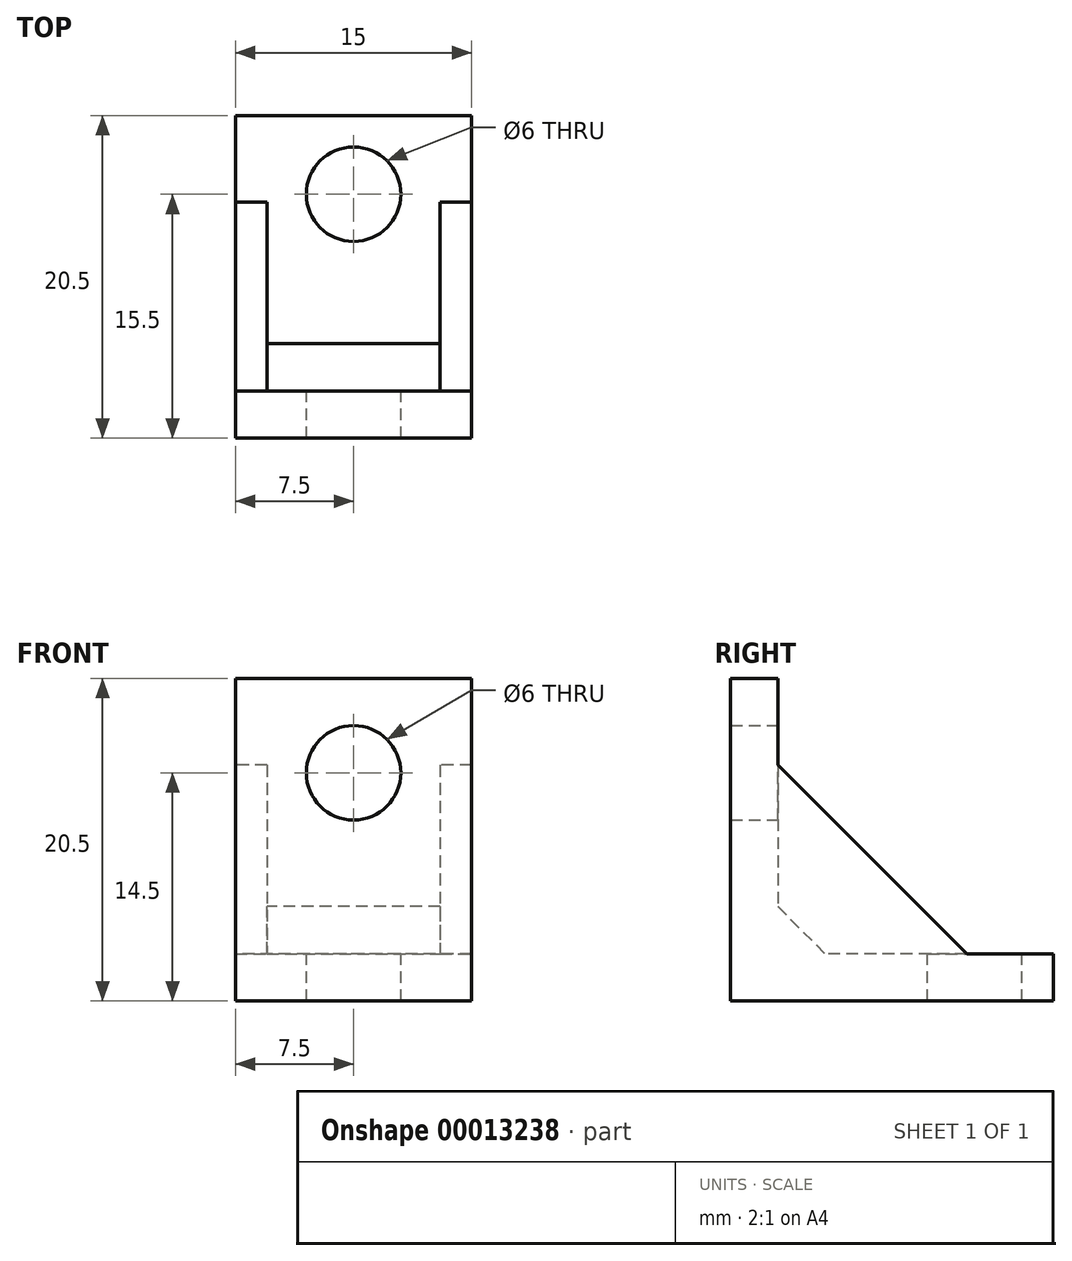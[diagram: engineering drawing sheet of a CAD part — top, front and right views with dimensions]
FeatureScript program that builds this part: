
annotation { "Feature Type Name" : "Feature", "Feature Type Description" : "" }
export const myFeature = defineFeature(function(context is Context, id is Id, definition is map)
    precondition{}
    {
        {
            var Q0;
            Q0=qCreatedBy(makeId("Right.planeOp"),FACE);
            var sketch = newSketch(context, id + "F0", { "sketchPlane" : qUnion([Q0])});
            skLineSegment(sketch, "E0", {"start": v(0, 20.5) * mm, "end": v(0, 0) * mm});
            skLineSegment(sketch, "E1", {"start": v(0, 0) * mm, "end": v(20.5, 0) * mm});
            skLineSegment(sketch, "E2", {"start": v(20.5, 0) * mm, "end": v(20.5, 3) * mm});
            skLineSegment(sketch, "E3", {"start": v(20.5, 3) * mm, "end": v(3, 3) * mm});
            skLineSegment(sketch, "E4", {"start": v(3, 3) * mm, "end": v(3, 20.5) * mm});
            skLineSegment(sketch, "E5", {"start": v(3, 20.5) * mm, "end": v(0, 20.5) * mm});
            skSolve(sketch);
        }
        {
            var Q0;
            Q0 = qSketchRegion(id + "F0", true);
            extrude(context, id + "F1", {"entities" : qUnion([Q0]), "depth" : 15 * mm});
        }
        {
            var Q0;
            Q0=makeQuery(id+"F1.opExtrude","SWEPT_FACE",FACE,{"disambiguationData":[OSD([sQuery(id+"F0.wireOp",EDGE,"E4")])]});
            var sketch = newSketch(context, id + "F2", { "sketchPlane" : qUnion([Q0])});
            skPoint(sketch, "E6", {"position": v(-7.5, 14.5) * mm});
            skPoint(sketch, "E7", {"position": v(-7.5, 20.5) * mm});
            skSolve(sketch);
        }
        {
            var Q0;
            Q0=makeQuery(id+"F1.opExtrude","SWEPT_FACE",FACE,{"disambiguationData":[OSD([sQuery(id+"F0.wireOp",EDGE,"E3")])]});
            var sketch = newSketch(context, id + "F3", { "sketchPlane" : qUnion([Q0])});
            skPoint(sketch, "E8", {"position": v(7.5, 15.5) * mm});
            skSolve(sketch);
        }
        {
            var Q0;
            Q0=sQuery(id+"F3.wireOp",VERTEX,"E8");
            var Q1;
            Q1=sQuery(id+"F2.wireOp",VERTEX,"E6");
            var Q2;
            Q2=makeQuery(id+"F1.opExtrude","SWEPT_BODY",BODY,{"disambiguationData":[OSD([sQuery(id+"F0.wireOp",EDGE,"E0"),sQuery(id+"F0.wireOp",EDGE,"E1"),sQuery(id+"F0.wireOp",EDGE,"E2"),sQuery(id+"F0.wireOp",EDGE,"E3"),sQuery(id+"F0.wireOp",EDGE,"E4"),sQuery(id+"F0.wireOp",EDGE,"E5")])]});
            hole(context, id + "F4", {"style" : HoleStyle.SIMPLE, "endStyle" : HoleEndStyle.THROUGH, "holeDiameter" : 6 * mm, "locations" : qUnion([Q0, Q1]), "scope" : qUnion([Q2]), "isTappedThrough" : true});
        }
        {
            var Q0;
            Q0=makeQuery(id+"F1.opExtrude","SWEPT_EDGE",EDGE,{"disambiguationData":[OSD([sQuery(id+"F0.wireOp",EDGE,"E3"),sQuery(id+"F0.wireOp",EDGE,"E4")])]});
            chamfer(context, id + "F5", {"entities" : qUnion([Q0]), "width" : 12 * mm, "tangentPropagation" : true});
        }
        {
            var Q0;
            Q0=makeQuery(id+"F1.opExtrude","SWEPT_FACE",FACE,{"disambiguationData":[OSD([sQuery(id+"F0.wireOp",EDGE,"E3")])]});
            var sketch = newSketch(context, id + "F6", { "sketchPlane" : qUnion([Q0])});
            skLineSegment(sketch, "E9.bottom", {"start": v(13, 20.5) * mm, "end": v(2, 20.5) * mm});
            skLineSegment(sketch, "E9.top", {"start": v(13, 3) * mm, "end": v(2, 3) * mm});
            skLineSegment(sketch, "E9.left", {"start": v(13, 20.5) * mm, "end": v(13, 3) * mm});
            skLineSegment(sketch, "E9.right", {"start": v(2, 20.5) * mm, "end": v(2, 3) * mm});
            skPoint(sketch, "E10", {"position": v(7.5, 20.5) * mm});
            skSolve(sketch);
        }
        {
            var Q0;
            Q0 = qSketchRegion(id + "F6", true);
            extrude(context, id + "F7", {"entities" : qUnion([Q0]), "operationType" : NewBodyOperationType.REMOVE, "endBound" : BoundingType.THROUGH_ALL, "depth" : 25 * mm});
        }
        {
            var Q0;
            Q0=makeQuery(id+"F7.boolean.opBoolean","COPY",EDGE,{"derivedFrom":makeQuery(id+"F7.opExtrude","CAP_EDGE",EDGE,{"disambiguationData":[OSD([sQuery(id+"F6.wireOp",EDGE,"E9.top")])],"isStart":true})});
            chamfer(context, id + "F8", {"entities" : qUnion([Q0]), "width" : 3 * mm, "tangentPropagation" : true});
        }
    });
